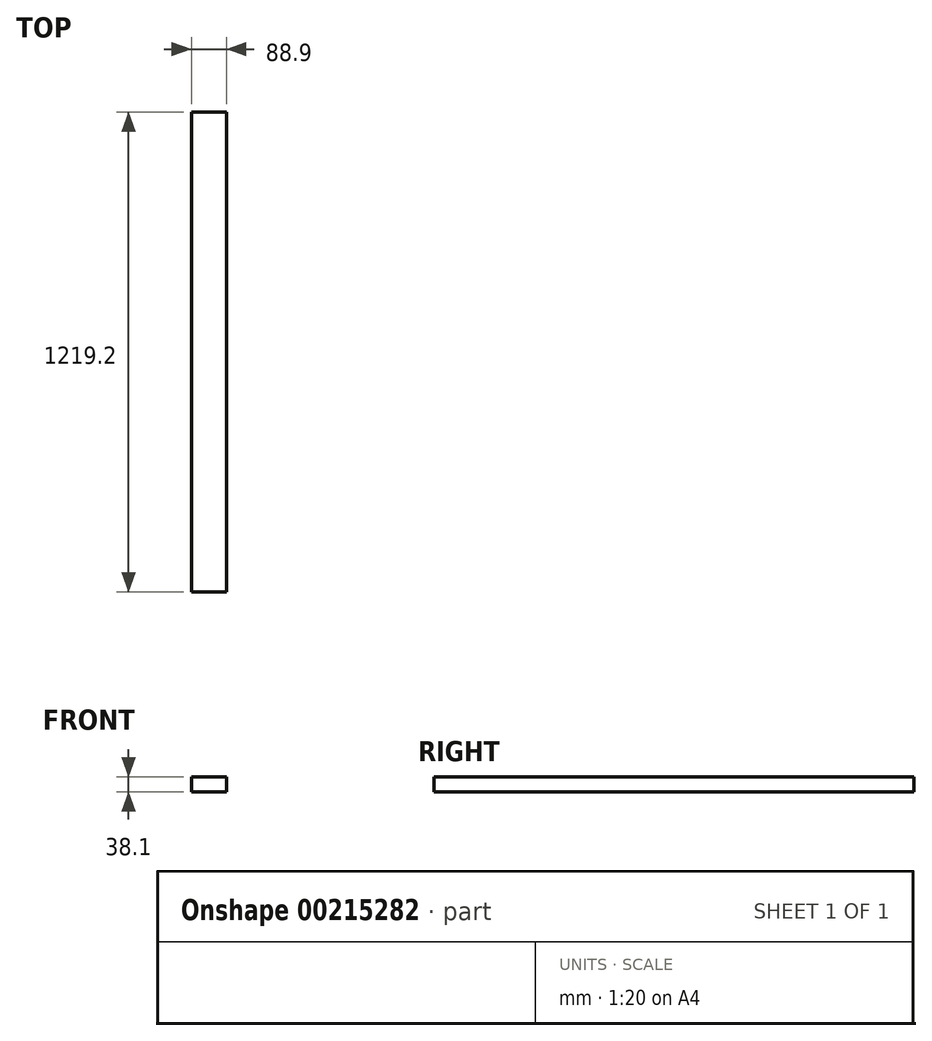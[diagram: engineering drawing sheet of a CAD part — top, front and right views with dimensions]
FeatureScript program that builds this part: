
annotation { "Feature Type Name" : "Feature", "Feature Type Description" : "" }
export const myFeature = defineFeature(function(context is Context, id is Id, definition is map)
    precondition{}
    {
        {
            var Q0;
            Q0=qCreatedBy(makeId("Top.planeOp"),FACE);
            var sketch = newSketch(context, id + "F0", { "sketchPlane" : qUnion([Q0])});
            skLineSegment(sketch, "E0.bottom", {"start": v(-44.45, 609.6) * mm, "end": v(44.45, 609.6) * mm});
            skLineSegment(sketch, "E0.top", {"start": v(-44.45, -609.6) * mm, "end": v(44.45, -609.6) * mm});
            skLineSegment(sketch, "E0.left", {"start": v(-44.45, 609.6) * mm, "end": v(-44.45, -609.6) * mm});
            skLineSegment(sketch, "E0.right", {"start": v(44.45, 609.6) * mm, "end": v(44.45, -609.6) * mm});
            skSolve(sketch);
        }
        {
            var Q0;
            Q0=makeQuery(id+"F0.imprint","IMPRINT",FACE,{"disambiguationData":[TD([[makeQuery(id+"F0.imprint","IMPRINT",EDGE,{"derivedFrom":sQuery(id+"F0.wireOp",EDGE,"E0.bottom")}),-1.0]])]});
            extrude(context, id + "F1", {"entities" : qUnion([Q0]), "depth" : 38.1 * mm});
        }
    });
